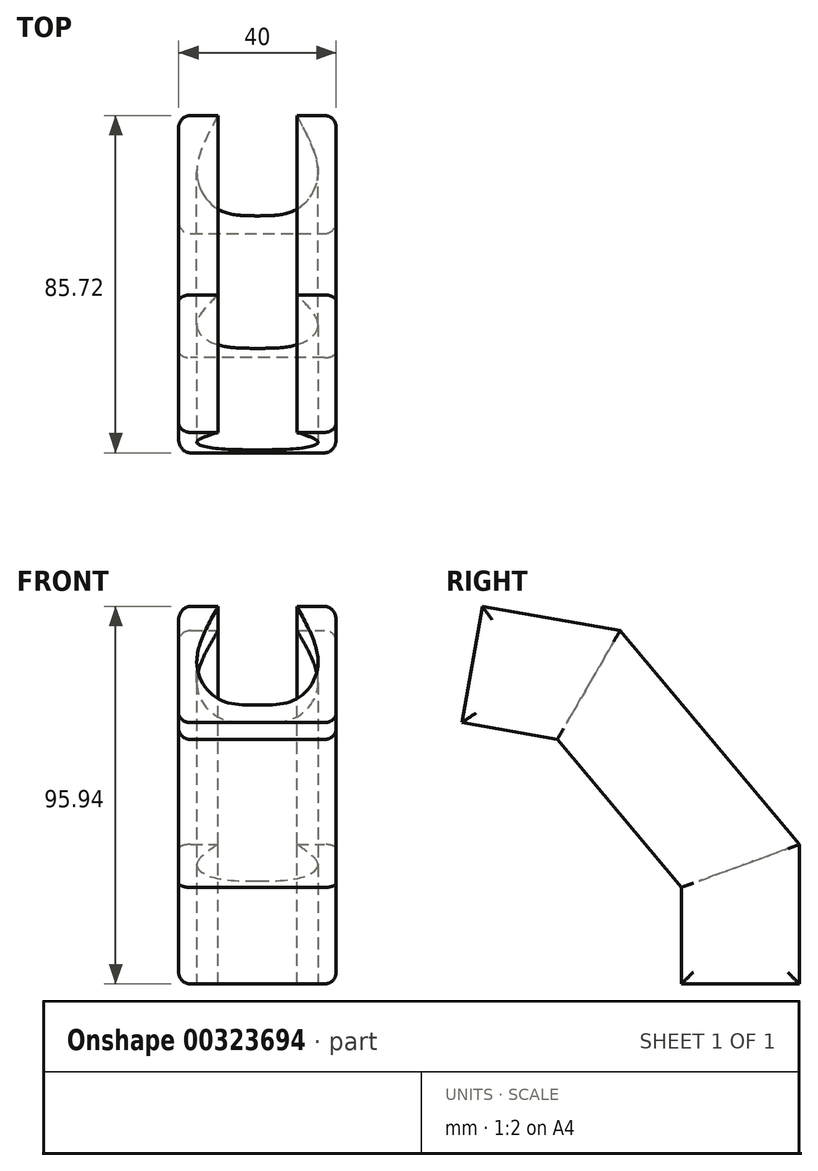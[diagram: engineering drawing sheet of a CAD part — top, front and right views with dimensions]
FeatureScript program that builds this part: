
annotation { "Feature Type Name" : "Feature", "Feature Type Description" : "" }
export const myFeature = defineFeature(function(context is Context, id is Id, definition is map)
    precondition{}
    {
        {
            var Q0;
            Q0=qCreatedBy(makeId("Top.planeOp"),FACE);
            var sketch = newSketch(context, id + "F0", { "sketchPlane" : qUnion([Q0])});
            skLineSegment(sketch, "E0.bottom", {"start": v(-20, 15) * mm, "end": v(-10, 15) * mm});
            skLineSegment(sketch, "E0.top", {"start": v(-20, -15) * mm, "end": v(20, -15) * mm});
            skLineSegment(sketch, "E0.left", {"start": v(-20, 15) * mm, "end": v(-20, -15) * mm});
            skLineSegment(sketch, "E0.right", {"start": v(20, 15) * mm, "end": v(20, -15) * mm});
            skPoint(sketch, "E0.middle", {"position": v(0, 0) * mm});
            skPoint(sketch, "E1", {"position": v(-10, 15) * mm});
            skPoint(sketch, "E2", {"position": v(10, 15) * mm});
            skFitSpline(sketch, "E3", {"points": [v(-10, 15) * mm, v(-15.39, 0) * mm, v(-10, -8.81) * mm, v(0, -10.5) * mm], "startDerivative": vector(-22.12, -40.44) * mm, "endDerivative": vector(34.8, -0.03) * mm});
            skPoint(sketch, "E4.endSnap0", {"position": v(0, 15) * mm});
            skFitSpline(sketch, "E5.MirrorCS", {"points": [v(10, 15) * mm, v(15.39, 0) * mm, v(10, -8.81) * mm, v(0, -10.5) * mm], "startDerivative": vector(22.12, -40.44) * mm, "endDerivative": vector(-34.8, -0.03) * mm});
            skLineSegment(sketch, "E6.trimOffspring", {"start": v(10, 15) * mm, "end": v(20, 15) * mm});
            skPoint(sketch, "E4.end.orphan", {"position": v(0, 4.34) * mm});
            skPoint(sketch, "E4.start.orphan", {"position": v(0, 15) * mm});
            skSolve(sketch);
        }
        {
            var Q0;
            Q0=qCreatedBy(makeId("Right.planeOp"),FACE);
            var sketch = newSketch(context, id + "F1", { "sketchPlane" : qUnion([Q0])});
            skLineSegment(sketch, "E7", {"start": v(0, 0) * mm, "end": v(0, 30) * mm});
            skLineSegment(sketch, "E8", {"start": v(0, 30) * mm, "end": v(-38.57, 75.96) * mm});
            skLineSegment(sketch, "E9", {"start": v(-38.57, 75.96) * mm, "end": v(-68.11, 81.17) * mm});
            skSolve(sketch);
        }
        {
            var Q0;
            Q0=makeQuery(id+"F0.imprint","IMPRINT",FACE,{"disambiguationData":[TD([[makeQuery(id+"F0.imprint","IMPRINT",EDGE,{"derivedFrom":sQuery(id+"F0.wireOp",EDGE,"E0.bottom")}),-1.0]])]});
            var Q1;
            Q1 = qConstructionFilter(qBodyType(qCreatedBy(id + "F1" ,EDGE), BodyType.WIRE), ConstructionObject.NO);
            sweep(context, id + "F2", {"profiles" : qUnion([Q0]), "path" : qUnion([Q1])});
        }
        {
            var Q0;
            Q0=makeQuery(id+"F2.opSweep","SWEPT_EDGE",EDGE,{"disambiguationData":[OSD([sQuery(id+"F0.wireOp",EDGE,"E0.bottom"),sQuery(id+"F0.wireOp",EDGE,"E0.left"),sQuery(id+"F1.wireOp",EDGE,"E7")])]});
            var Q1;
            Q1=makeQuery(id+"F2.opSweep","SWEPT_EDGE",EDGE,{"disambiguationData":[OSD([sQuery(id+"F0.wireOp",EDGE,"E0.bottom"),sQuery(id+"F0.wireOp",EDGE,"E0.left"),sQuery(id+"F1.wireOp",EDGE,"E8")])]});
            var Q2;
            Q2=makeQuery(id+"F2.opSweep","SWEPT_EDGE",EDGE,{"disambiguationData":[OSD([sQuery(id+"F0.wireOp",EDGE,"E0.bottom"),sQuery(id+"F0.wireOp",EDGE,"E0.left"),sQuery(id+"F1.wireOp",EDGE,"E9")])]});
            var Q3;
            Q3=makeQuery(id+"F2.opSweep","CAP_EDGE",EDGE,{"disambiguationData":[OSD([sQuery(id+"F0.wireOp",EDGE,"E0.left"),sQuery(id+"F1.wireOp",VERTEX,"E9.end")])],"isStart":false});
            var Q4;
            Q4=makeQuery(id+"F2.opSweep","SWEPT_EDGE",EDGE,{"disambiguationData":[OSD([sQuery(id+"F0.wireOp",EDGE,"E0.top"),sQuery(id+"F0.wireOp",EDGE,"E0.left"),sQuery(id+"F1.wireOp",EDGE,"E9")])]});
            var Q5;
            Q5=makeQuery(id+"F2.opSweep","SWEPT_EDGE",EDGE,{"disambiguationData":[OSD([sQuery(id+"F0.wireOp",EDGE,"E0.top"),sQuery(id+"F0.wireOp",EDGE,"E0.left"),sQuery(id+"F1.wireOp",EDGE,"E8")])]});
            var Q6;
            Q6=makeQuery(id+"F2.opSweep","SWEPT_EDGE",EDGE,{"disambiguationData":[OSD([sQuery(id+"F0.wireOp",EDGE,"E0.top"),sQuery(id+"F0.wireOp",EDGE,"E0.left"),sQuery(id+"F1.wireOp",EDGE,"E7")])]});
            var Q7;
            Q7=makeQuery(id+"F2.opSweep","CAP_EDGE",EDGE,{"disambiguationData":[OSD([sQuery(id+"F0.wireOp",EDGE,"E0.left"),sQuery(id+"F1.wireOp",VERTEX,"E7.start")])],"isStart":true});
            var Q8;
            Q8=makeQuery(id+"F2.opSweep","SWEPT_EDGE",EDGE,{"disambiguationData":[OSD([sQuery(id+"F0.wireOp",EDGE,"E0.right"),sQuery(id+"F0.wireOp",EDGE,"E6.trimOffspring"),sQuery(id+"F1.wireOp",EDGE,"E9")])]});
            var Q9;
            Q9=makeQuery(id+"F2.opSweep","SWEPT_EDGE",EDGE,{"disambiguationData":[OSD([sQuery(id+"F0.wireOp",EDGE,"E0.right"),sQuery(id+"F0.wireOp",EDGE,"E6.trimOffspring"),sQuery(id+"F1.wireOp",EDGE,"E8")])]});
            var Q10;
            Q10=makeQuery(id+"F2.opSweep","SWEPT_EDGE",EDGE,{"disambiguationData":[OSD([sQuery(id+"F0.wireOp",EDGE,"E0.right"),sQuery(id+"F0.wireOp",EDGE,"E6.trimOffspring"),sQuery(id+"F1.wireOp",EDGE,"E7")])]});
            var Q11;
            Q11=makeQuery(id+"F2.opSweep","CAP_EDGE",EDGE,{"disambiguationData":[OSD([sQuery(id+"F0.wireOp",EDGE,"E0.right"),sQuery(id+"F1.wireOp",VERTEX,"E7.start")])],"isStart":true});
            var Q12;
            Q12=makeQuery(id+"F2.opSweep","SWEPT_EDGE",EDGE,{"disambiguationData":[OSD([sQuery(id+"F0.wireOp",EDGE,"E0.top"),sQuery(id+"F0.wireOp",EDGE,"E0.right"),sQuery(id+"F1.wireOp",EDGE,"E7")])]});
            var Q13;
            Q13=makeQuery(id+"F2.opSweep","SWEPT_EDGE",EDGE,{"disambiguationData":[OSD([sQuery(id+"F0.wireOp",EDGE,"E0.top"),sQuery(id+"F0.wireOp",EDGE,"E0.right"),sQuery(id+"F1.wireOp",EDGE,"E8")])]});
            var Q14;
            Q14=makeQuery(id+"F2.opSweep","SWEPT_EDGE",EDGE,{"disambiguationData":[OSD([sQuery(id+"F0.wireOp",EDGE,"E0.top"),sQuery(id+"F0.wireOp",EDGE,"E0.right"),sQuery(id+"F1.wireOp",EDGE,"E9")])]});
            var Q15;
            Q15=makeQuery(id+"F2.opSweep","CAP_EDGE",EDGE,{"disambiguationData":[OSD([sQuery(id+"F0.wireOp",EDGE,"E0.right"),sQuery(id+"F1.wireOp",VERTEX,"E9.end")])],"isStart":false});
            fillet(context, id + "F3", {"entities" : qUnion([Q0, Q1, Q2, Q3, Q4, Q5, Q6, Q7, Q8, Q9, Q10, Q11, Q12, Q13, Q14, Q15]), "radius" : 3 * mm, "tangentPropagation" : true, "allowEdgeOverflow" : false});
        }
    });
